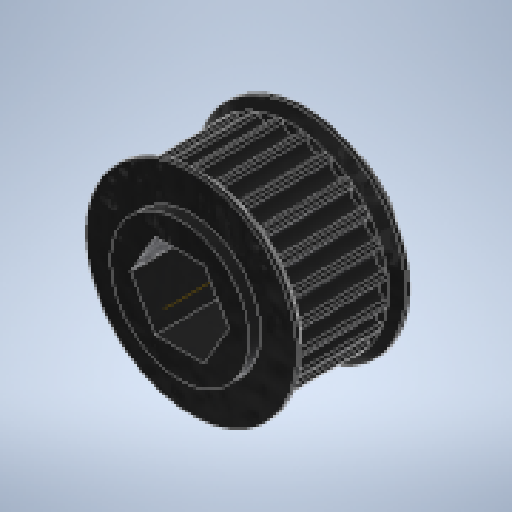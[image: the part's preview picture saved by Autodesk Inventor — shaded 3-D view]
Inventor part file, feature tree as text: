
AUTODESK INVENTOR PART (.ipt)
format: ipt  version: 2023.3 (Build 273359000, 359)  size: 351,744 bytes
history: native  units: in
note: dims shown in document units (in); Inventor stores cm internally (conversion verified against a paired STEP export)
features: extrude x8, sketch x7, mirror x2, chamfer x2, other x1, fillet x1, pattern_circular x1, projected_geometry x1
ambient origin geometry x8: Origin, YZ Plane, XZ Plane, XY Plane, X Axis, Y Axis, Z Axis, Center Point
bodies: Solid1 (feature_tree)
feature tree (23):
  other  "Hex Bore"
  extrude  "HTD Base"  Depth=0.3937in TaperAngle=0.0deg
  extrude  "HTD Flange"  Depth=0.0591in
  mirror  "HTD Flanges"
  chamfer  "HTD Flange Chamfer"  Distance=0.0787in Angle=45.0deg
  extrude  "GT2 Base"  TaperAngle=0.0deg  [1 undecoded]
  extrude  "GT2 Base Tooth"  TaperAngle=0.0deg  [1 undecoded]
  fillet  "GT2 Base Tooth pt. 2"  Radius=0.8723in
  pattern_circular  "GT2 Teeth"  [2 undecoded]
  extrude  "GT2 Flange"  Depth=0.5638in
  mirror  "GT2 Flanges"
  chamfer  "GT2 Flange Chamfer"  Distance=0.0075in
  extrude  "Circle Bore"  TaperAngle=0.0deg  [1 undecoded]
  sketch  "Sketch9"  dims[d25=0.3937in d26=0.0in d27=0.0727in d28=0.0075in d29=0.0in d30=0.0in d31=0.0118in d32=9.4488in d33=360.0deg d35=0.0394in d36=0.0591in d37=0.0in d38=0.0394in d39=0.0787in d40=45.0deg d41=0.625in d42=0.125in d43=0.0in d44=0.5638in d45=0.0in]
  extrude  "Extrusion10"  Depth=0.0118in
  extrude  "Extrusion9"  Depth=0.5638in
  sketch  "Sketch1"  dims[d0=1.4588in d1=0.3937in d2=0.0in]
  sketch  "Sketch4"  dims[d12=0.0394in d13=0.0591in]
  sketch  "Sketch5"  dims[d14=0.0in]
  sketch  "Sketch6"  dims[d15=0.0394in d16=0.0787in d17=45.0deg]
  sketch  "Sketch7"  dims[d18=0.385in d19=0.0in d20=0.0in]
  sketch  "Sketch8"  dims[d21=0.385in d22=0.0in d23=0.0in d24=0.8723in]
  projected_geometry  "Projected Loop1"
note: 5 required parameter values undecoded (feature->parameter linkage not recoverable at this tier; creation-order binding heuristic only, values carry confidence <= 0.55)
